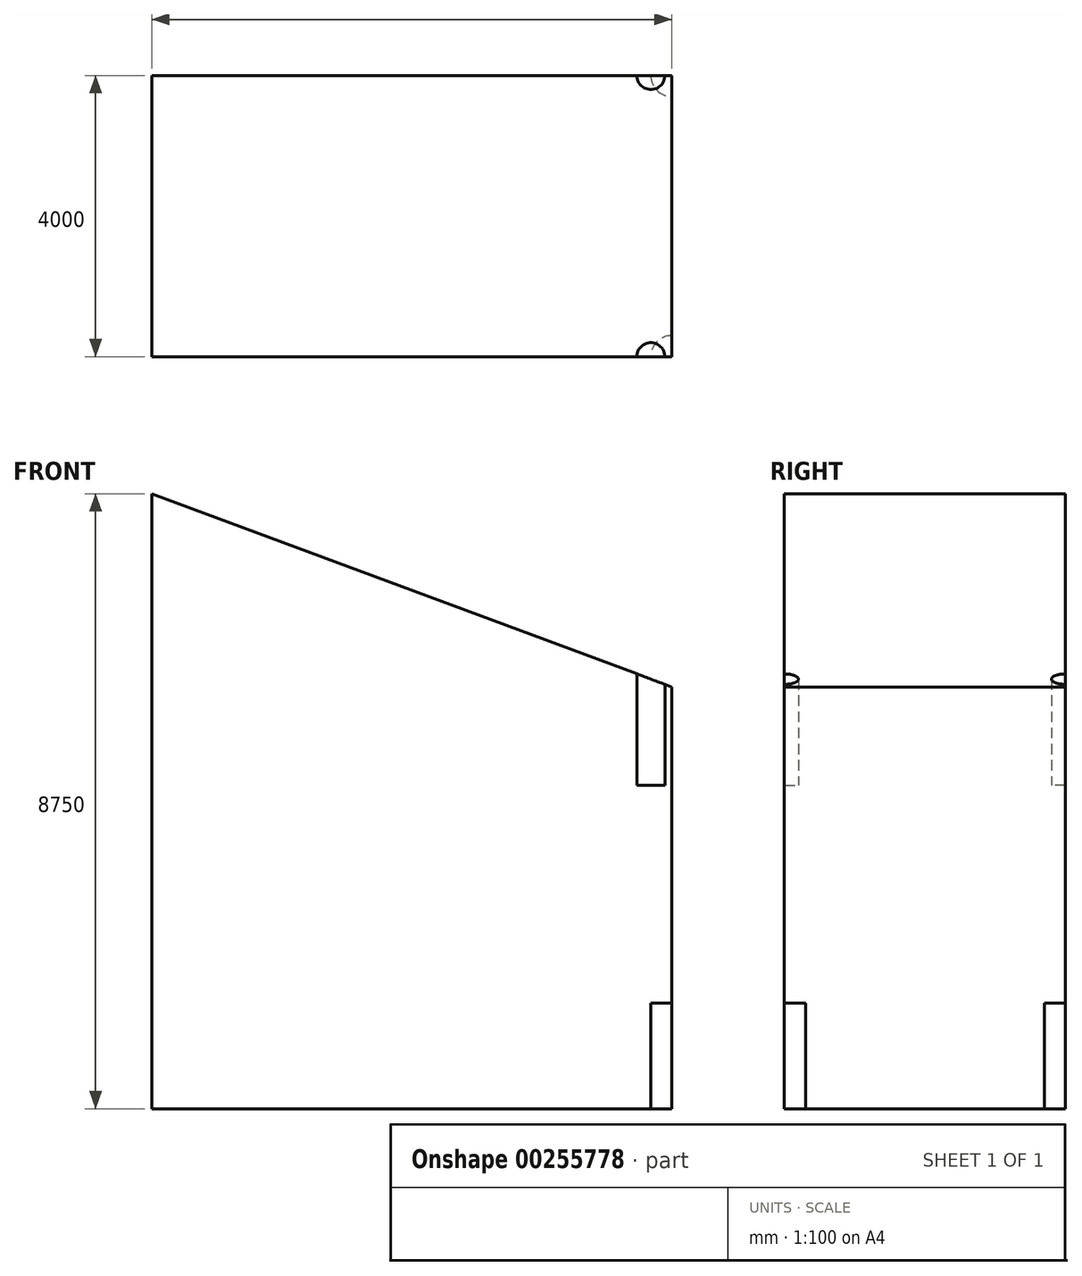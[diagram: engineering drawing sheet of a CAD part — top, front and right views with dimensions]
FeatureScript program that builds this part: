
annotation { "Feature Type Name" : "Feature", "Feature Type Description" : "" }
export const myFeature = defineFeature(function(context is Context, id is Id, definition is map)
    precondition{}
    {
        {
            var Q0;
            Q0=qCreatedBy(makeId("Front.planeOp"),FACE);
            var sketch = newSketch(context, id + "F0", { "sketchPlane" : qUnion([Q0])});
            skLineSegment(sketch, "E0", {"start": v(0, 0) * mm, "end": v(-7400, 0) * mm});
            skLineSegment(sketch, "E1", {"start": v(-7400, 0) * mm, "end": v(-7400, 8750) * mm});
            skLineSegment(sketch, "E2", {"start": v(-7400, 8750) * mm, "end": v(0, 6000) * mm});
            skLineSegment(sketch, "E3", {"start": v(0, 6000) * mm, "end": v(0, 0) * mm});
            skSolve(sketch);
        }
        {
            var Q0;
            Q0=makeQuery(id+"F0.imprint","IMPRINT",FACE,{"disambiguationData":[TD([[makeQuery(id+"F0.imprint","IMPRINT",EDGE,{"derivedFrom":sQuery(id+"F0.wireOp",EDGE,"E0")}),-1.0]])]});
            extrude(context, id + "F1", {"entities" : qUnion([Q0]), "oppositeDirection" : true, "depth" : 4000 * mm});
        }
        {
            var Q0;
            Q0=makeQuery(id+"F1.opExtrude","SWEPT_FACE",FACE,{"disambiguationData":[OSD([sQuery(id+"F0.wireOp",EDGE,"E0")])]});
            var sketch = newSketch(context, id + "F2", { "sketchPlane" : qUnion([Q0])});
            skCircle(sketch, "E4", {"center": v(0, 0) * mm, "radius": 300 * mm});
            skCircle(sketch, "E5", {"center": v(0, -4000) * mm, "radius": 300 * mm});
            skSolve(sketch);
        }
        {
            var Q0;
            Q0 = qSketchRegion(id + "F2", true);
            extrude(context, id + "F3", {"entities" : qUnion([Q0]), "operationType" : NewBodyOperationType.REMOVE, "oppositeDirection" : true, "depth" : 1500 * mm});
        }
        {
            var Q0;
            Q0=makeQuery(id+"F1.opExtrude","SWEPT_FACE",FACE,{"disambiguationData":[OSD([sQuery(id+"F0.wireOp",EDGE,"E0")])]});
            cPlane(context, id + "F4", {"entities" : qUnion([Q0]), "cplaneType" : CPlaneType.OFFSET, "offset" : 4600 * mm, "oppositeDirection" : true, "width" : 150 * mm, "height" : 150 * mm});
        }
        {
            var Q0;
            Q0=qCreatedBy(id+"F4.planeOp",FACE);
            var sketch = newSketch(context, id + "F5", { "sketchPlane" : qUnion([Q0])});
            skCircle(sketch, "E6", {"center": v(-300, 0) * mm, "radius": 200 * mm});
            skPoint(sketch, "E7.0", {"position": v(0, -4000) * mm});
            skCircle(sketch, "E8", {"center": v(-300, -4000) * mm, "radius": 200 * mm});
            skSolve(sketch);
        }
        {
            var Q0;
            Q0 = qSketchRegion(id + "F5", true);
            var Q1;
            Q1=makeQuery(id+"F1.opExtrude","SWEPT_FACE",FACE,{"disambiguationData":[OSD([sQuery(id+"F0.wireOp",EDGE,"E2")])]});
            extrude(context, id + "F6", {"entities" : qUnion([Q0]), "operationType" : NewBodyOperationType.REMOVE, "endBound" : BoundingType.UP_TO_SURFACE, "oppositeDirection" : true, "endBoundEntityFace" : qUnion([Q1]), "depth" : 25 * mm});
        }
    });
